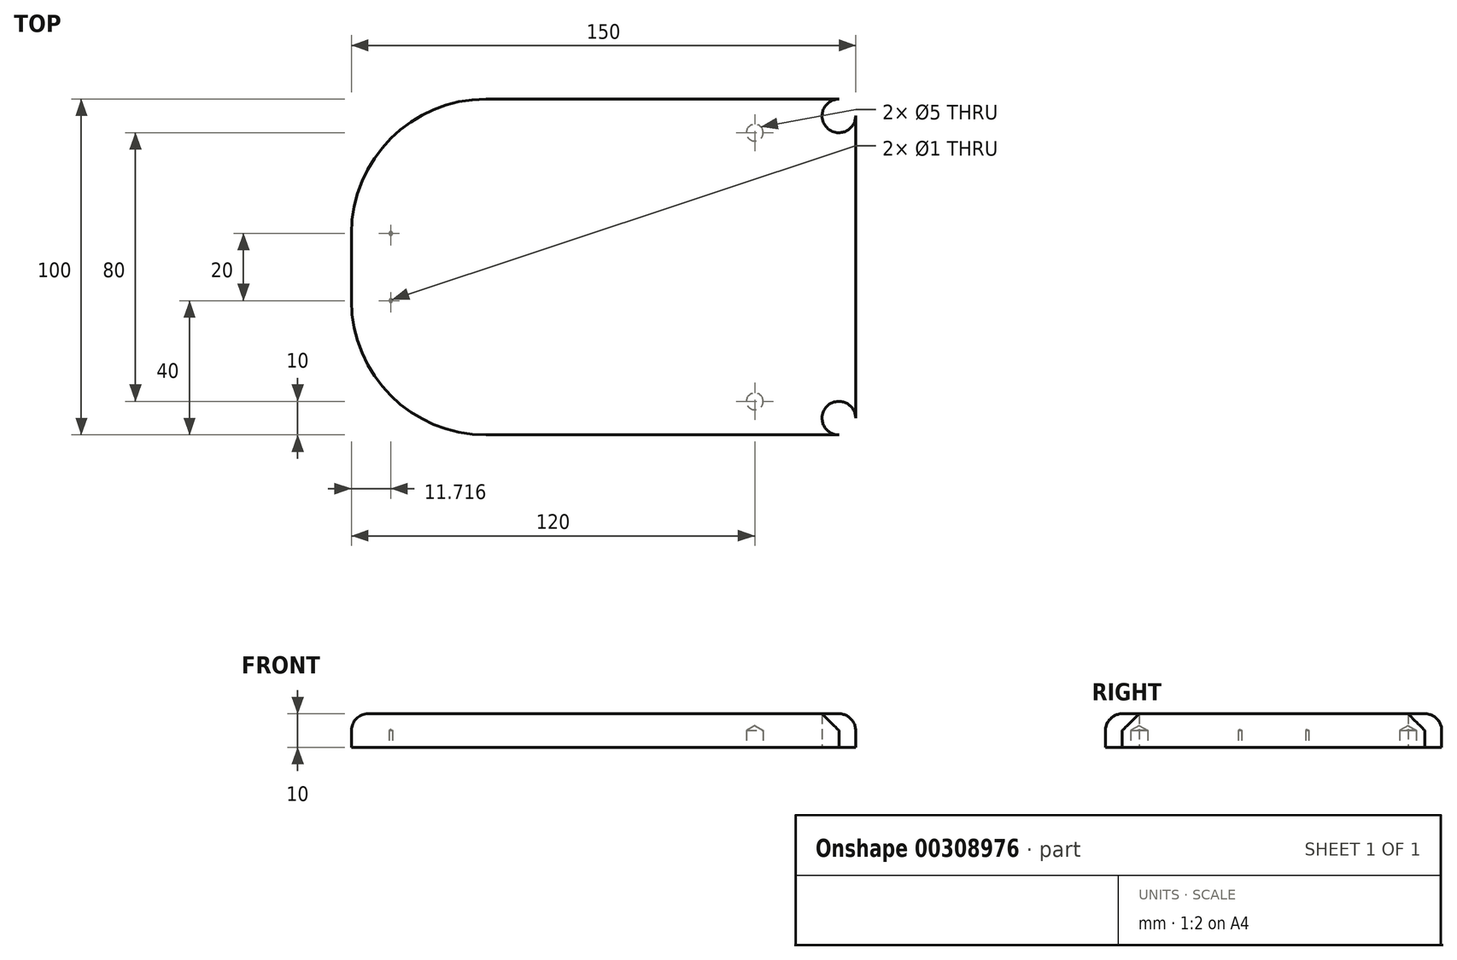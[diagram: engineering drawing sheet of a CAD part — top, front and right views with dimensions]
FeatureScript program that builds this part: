
annotation { "Feature Type Name" : "Feature", "Feature Type Description" : "" }
export const myFeature = defineFeature(function(context is Context, id is Id, definition is map)
    precondition{}
    {
        {
            var Q0;
            Q0=qCreatedBy(makeId("Top.planeOp"),FACE);
            var sketch = newSketch(context, id + "F0", { "sketchPlane" : qUnion([Q0])});
            skLineSegment(sketch, "E0.bottom", {"start": v(0, 0) * mm, "end": v(-110, 0) * mm});
            skLineSegment(sketch, "E0.top", {"start": v(0, 100) * mm, "end": v(-110, 100) * mm});
            skLineSegment(sketch, "E0.left", {"start": v(0, 0) * mm, "end": v(0, 100) * mm});
            skLineSegment(sketch, "E0.right", {"start": v(-150, 40) * mm, "end": v(-150, 60) * mm});
            skPoint(sketch, "E1.visualSharp", {"position": v(-150, 100) * mm});
            skArc(sketch, "E1.filletArc", {"start": v(-110, 100) * mm, "mid": v(-138.28, 88.28) * mm, "end": v(-150, 60) * mm});
            skPoint(sketch, "E2.visualSharp", {"position": v(-150, 0) * mm});
            skArc(sketch, "E2.filletArc", {"start": v(-150, 40) * mm, "mid": v(-138.28, 11.72) * mm, "end": v(-110, 0) * mm});
            skLineSegment(sketch, "E3", {"start": v(-5, 104.43) * mm, "end": v(-5, 100) * mm});
            skCircle(sketch, "E4", {"center": v(-5, 95) * mm, "radius": 5 * mm});
            skCircle(sketch, "E5", {"center": v(-5, 5) * mm, "radius": 5 * mm});
            skSolve(sketch);
        }
        {
            var Q0;
            Q0=makeQuery(id+"F0.imprint","IMPRINT",FACE,{"disambiguationData":[TD([[makeQuery(id+"F0.imprint","IMPRINT",EDGE,{"derivedFrom":sQuery(id+"F0.wireOp",EDGE,"E0.right")}),-1.0]])]});
            extrude(context, id + "F1", {"entities" : qUnion([Q0]), "depth" : 10 * mm});
        }
        {
            var Q0;
            Q0=makeQuery(id+"F1.opExtrude","CAP_FACE",FACE,{"disambiguationData":[OSD([sQuery(id+"F0.wireOp",EDGE,"E0.bottom"),sQuery(id+"F0.wireOp",EDGE,"E0.top"),sQuery(id+"F0.wireOp",EDGE,"E0.left"),sQuery(id+"F0.wireOp",EDGE,"E0.right"),sQuery(id+"F0.wireOp",EDGE,"E1.filletArc"),sQuery(id+"F0.wireOp",EDGE,"E2.filletArc"),sQuery(id+"F0.wireOp",EDGE,"E4"),sQuery(id+"F0.wireOp",EDGE,"E5")])],"isStart":true});
            var sketch = newSketch(context, id + "F2", { "sketchPlane" : qUnion([Q0])});
            skCircle(sketch, "E6", {"center": v(-30, -10) * mm, "radius": 2.5 * mm});
            skCircle(sketch, "E7", {"center": v(-30, -90) * mm, "radius": 2.5 * mm});
            skSolve(sketch);
        }
        {
            var Q0;
            Q0=sQuery(id+"F2.wireOp",VERTEX,"E6.center");
            var Q1;
            Q1=sQuery(id+"F2.wireOp",VERTEX,"E7.center");
            var Q2;
            Q2=makeQuery(id+"F1.opExtrude","SWEPT_BODY",BODY,{"disambiguationData":[OSD([sQuery(id+"F0.wireOp",EDGE,"E0.bottom"),sQuery(id+"F0.wireOp",EDGE,"E0.top"),sQuery(id+"F0.wireOp",EDGE,"E0.left"),sQuery(id+"F0.wireOp",EDGE,"E0.right"),sQuery(id+"F0.wireOp",EDGE,"E1.filletArc"),sQuery(id+"F0.wireOp",EDGE,"E2.filletArc"),sQuery(id+"F0.wireOp",EDGE,"E4"),sQuery(id+"F0.wireOp",EDGE,"E5")])]});
            hole(context, id + "F3", {"style" : HoleStyle.SIMPLE, "endStyle" : HoleEndStyle.BLIND, "holeDiameter" : 5 * mm, "holeDepth" : 5 * mm, "tappedDepth" : 12 * mm, "tapClearance" : 3, "locations" : qUnion([Q0, Q1]), "scope" : qUnion([Q2])});
        }
        {
            var Q0;
            Q0=makeQuery(id+"F1.opExtrude","CAP_FACE",FACE,{"disambiguationData":[OSD([sQuery(id+"F0.wireOp",EDGE,"E0.bottom"),sQuery(id+"F0.wireOp",EDGE,"E0.top"),sQuery(id+"F0.wireOp",EDGE,"E0.left"),sQuery(id+"F0.wireOp",EDGE,"E0.right"),sQuery(id+"F0.wireOp",EDGE,"E1.filletArc"),sQuery(id+"F0.wireOp",EDGE,"E2.filletArc"),sQuery(id+"F0.wireOp",EDGE,"E4"),sQuery(id+"F0.wireOp",EDGE,"E5")])],"isStart":true});
            var sketch = newSketch(context, id + "F4", { "sketchPlane" : qUnion([Q0])});
            skLineSegment(sketch, "E8", {"start": v(-138.28, -1.78) * mm, "end": v(-138.28, -94.26) * mm});
            skPoint(sketch, "E8.startSnap0", {"position": v(-138.28, -11.72) * mm});
            skPoint(sketch, "E8.endSnap0", {"position": v(-138.28, -88.28) * mm});
            skLineSegment(sketch, "E9", {"start": v(-158.64, -40) * mm, "end": v(-108.54, -40) * mm});
            skLineSegment(sketch, "E10", {"start": v(-157.67, -60) * mm, "end": v(-105.41, -60) * mm});
            skCircle(sketch, "E11", {"center": v(-138.28, -40) * mm, "radius": 2.5 * mm});
            skCircle(sketch, "E12", {"center": v(-138.28, -60) * mm, "radius": 2.5 * mm});
            skSolve(sketch);
        }
        {
            var Q0;
            Q0=sQuery(id+"F4.wireOp",VERTEX,"E11.center");
            var Q1;
            Q1=sQuery(id+"F4.wireOp",VERTEX,"E12.center");
            var Q2;
            Q2=makeQuery(id+"F1.opExtrude","SWEPT_BODY",BODY,{"disambiguationData":[OSD([sQuery(id+"F0.wireOp",EDGE,"E0.bottom"),sQuery(id+"F0.wireOp",EDGE,"E0.top"),sQuery(id+"F0.wireOp",EDGE,"E0.left"),sQuery(id+"F0.wireOp",EDGE,"E0.right"),sQuery(id+"F0.wireOp",EDGE,"E1.filletArc"),sQuery(id+"F0.wireOp",EDGE,"E2.filletArc"),sQuery(id+"F0.wireOp",EDGE,"E4"),sQuery(id+"F0.wireOp",EDGE,"E5")])]});
            hole(context, id + "F5", {"style" : HoleStyle.SIMPLE, "endStyle" : HoleEndStyle.BLIND, "holeDiameter" : 1 * mm, "holeDepth" : 5 * mm, "tappedDepth" : 12 * mm, "tapClearance" : 3, "locations" : qUnion([Q0, Q1]), "scope" : qUnion([Q2])});
        }
        {
            var Q0;
            Q0=makeQuery(id+"F1.opExtrude","CAP_EDGE",EDGE,{"disambiguationData":[OSD([sQuery(id+"F0.wireOp",EDGE,"E0.top")])],"isStart":false});
            var Q1;
            Q1=makeQuery(id+"F1.opExtrude","CAP_EDGE",EDGE,{"disambiguationData":[OSD([sQuery(id+"F0.wireOp",EDGE,"E0.left")])],"isStart":false});
            fillet(context, id + "F6", {"entities" : qUnion([Q0, Q1]), "radius" : 5 * mm, "tangentPropagation" : true, "allowEdgeOverflow" : false});
        }
    });
